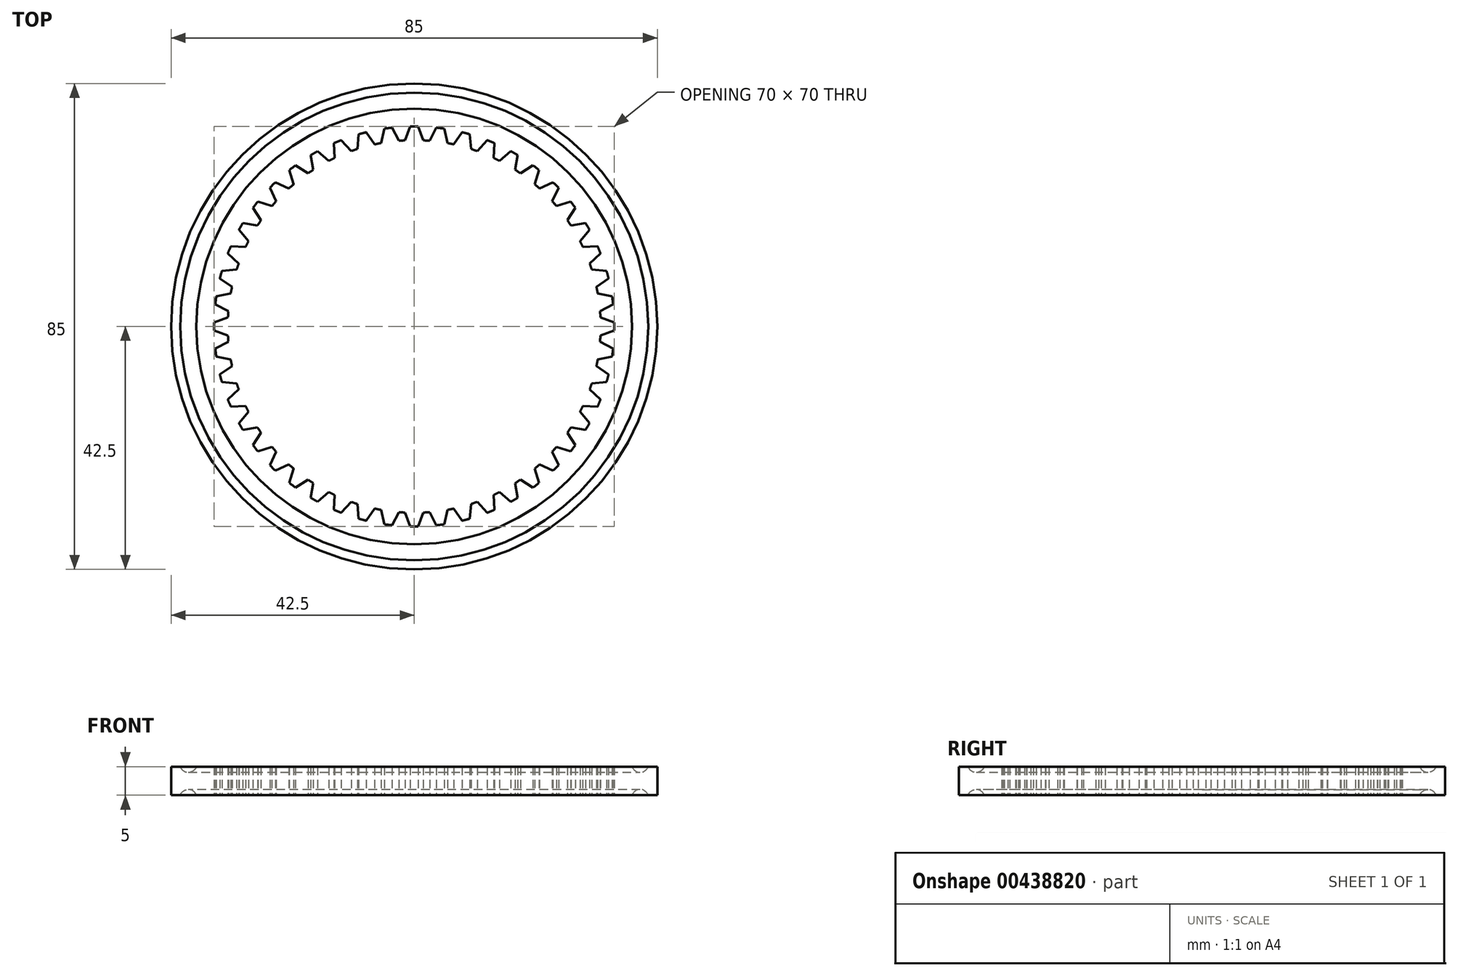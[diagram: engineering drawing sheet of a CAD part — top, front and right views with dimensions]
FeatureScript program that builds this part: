
annotation { "Feature Type Name" : "Feature", "Feature Type Description" : "" }
export const myFeature = defineFeature(function(context is Context, id is Id, definition is map)
    precondition{}
    {
        {
            var Q0;
            Q0=qCreatedBy(makeId("Top.planeOp"),FACE);
            var sketch = newSketch(context, id + "F0", { "sketchPlane" : qUnion([Q0])});
            skCircle(sketch, "E0", {"center": v(0, 0) * mm, "radius": 42.5 * mm});
            skCircle(sketch, "E1", {"center": v(0, 0) * mm, "radius": 34 * mm, "construction": true});
            skCircle(sketch, "E2", {"center": v(0, 0) * mm, "radius": 32.6 * mm, "construction": true});
            skCircle(sketch, "E3", {"center": v(0, 0) * mm, "radius": 35 * mm, "construction": true});
            skLineSegment(sketch, "E4", {"start": v(-1.57, 32.56) * mm, "end": v(-0.69, 35) * mm});
            skLineSegment(sketch, "E5.MirrorCS", {"start": v(1.57, 32.56) * mm, "end": v(0.69, 35) * mm});
            skLineSegment(sketch, "E6.1.0", {"start": v(-5.8, 32.08) * mm, "end": v(-5.25, 34.6) * mm});
            skLineSegment(sketch, "E6.1.1", {"start": v(-2.7, 32.49) * mm, "end": v(-3.89, 34.78) * mm});
            skLineSegment(sketch, "E7.1.2.0", {"start": v(-9.94, 31.05) * mm, "end": v(-9.72, 33.62) * mm});
            skLineSegment(sketch, "E7.3.2.0", {"start": v(-6.91, 31.86) * mm, "end": v(-8.4, 33.98) * mm});
            skLineSegment(sketch, "E7.1.3.0", {"start": v(-13.91, 29.48) * mm, "end": v(-14.03, 32.07) * mm});
            skLineSegment(sketch, "E7.3.3.0", {"start": v(-11, 30.68) * mm, "end": v(-12.76, 32.6) * mm});
            skLineSegment(sketch, "E7.1.4.0", {"start": v(-17.64, 27.41) * mm, "end": v(-18.1, 29.96) * mm});
            skLineSegment(sketch, "E7.3.4.0", {"start": v(-14.92, 28.99) * mm, "end": v(-16.9, 30.65) * mm});
            skLineSegment(sketch, "E7.1.5.0", {"start": v(-21.07, 24.88) * mm, "end": v(-21.85, 27.34) * mm});
            skLineSegment(sketch, "E7.3.5.0", {"start": v(-18.58, 26.79) * mm, "end": v(-20.76, 28.18) * mm});
            skLineSegment(sketch, "E7.1.6.0", {"start": v(-24.14, 21.91) * mm, "end": v(-25.23, 24.26) * mm});
            skLineSegment(sketch, "E7.3.6.0", {"start": v(-21.91, 24.14) * mm, "end": v(-24.26, 25.23) * mm});
            skLineSegment(sketch, "E7.1.7.0", {"start": v(-26.79, 18.58) * mm, "end": v(-28.18, 20.76) * mm});
            skLineSegment(sketch, "E7.3.7.0", {"start": v(-24.88, 21.07) * mm, "end": v(-27.34, 21.85) * mm});
            skLineSegment(sketch, "E7.1.8.0", {"start": v(-28.99, 14.92) * mm, "end": v(-30.65, 16.9) * mm});
            skLineSegment(sketch, "E7.3.8.0", {"start": v(-27.41, 17.64) * mm, "end": v(-29.96, 18.1) * mm});
            skLineSegment(sketch, "E7.1.9.0", {"start": v(-30.68, 11) * mm, "end": v(-32.6, 12.76) * mm});
            skLineSegment(sketch, "E7.3.9.0", {"start": v(-29.48, 13.91) * mm, "end": v(-32.07, 14.03) * mm});
            skLineSegment(sketch, "E7.1.10.0", {"start": v(-31.86, 6.91) * mm, "end": v(-33.98, 8.4) * mm});
            skLineSegment(sketch, "E7.3.10.0", {"start": v(-31.05, 9.94) * mm, "end": v(-33.62, 9.72) * mm});
            skLineSegment(sketch, "E7.1.11.0", {"start": v(-32.49, 2.7) * mm, "end": v(-34.78, 3.89) * mm});
            skLineSegment(sketch, "E7.3.11.0", {"start": v(-32.08, 5.8) * mm, "end": v(-34.6, 5.25) * mm});
            skLineSegment(sketch, "E7.1.12.0", {"start": v(-32.56, -1.57) * mm, "end": v(-35, -0.69) * mm});
            skLineSegment(sketch, "E7.3.12.0", {"start": v(-32.56, 1.57) * mm, "end": v(-35, 0.69) * mm});
            skLineSegment(sketch, "E7.1.13.0", {"start": v(-32.08, -5.8) * mm, "end": v(-34.6, -5.25) * mm});
            skLineSegment(sketch, "E7.3.13.0", {"start": v(-32.49, -2.7) * mm, "end": v(-34.78, -3.89) * mm});
            skLineSegment(sketch, "E7.1.14.0", {"start": v(-31.05, -9.94) * mm, "end": v(-33.62, -9.72) * mm});
            skLineSegment(sketch, "E7.3.14.0", {"start": v(-31.86, -6.91) * mm, "end": v(-33.98, -8.4) * mm});
            skLineSegment(sketch, "E7.1.15.0", {"start": v(-29.48, -13.91) * mm, "end": v(-32.07, -14.03) * mm});
            skLineSegment(sketch, "E7.3.15.0", {"start": v(-30.68, -11) * mm, "end": v(-32.6, -12.76) * mm});
            skLineSegment(sketch, "E7.1.16.0", {"start": v(-27.41, -17.64) * mm, "end": v(-29.96, -18.1) * mm});
            skLineSegment(sketch, "E7.3.16.0", {"start": v(-28.99, -14.92) * mm, "end": v(-30.65, -16.9) * mm});
            skLineSegment(sketch, "E7.1.17.0", {"start": v(-24.88, -21.07) * mm, "end": v(-27.34, -21.85) * mm});
            skLineSegment(sketch, "E7.3.17.0", {"start": v(-26.79, -18.58) * mm, "end": v(-28.18, -20.76) * mm});
            skLineSegment(sketch, "E7.1.18.0", {"start": v(-21.91, -24.14) * mm, "end": v(-24.26, -25.23) * mm});
            skLineSegment(sketch, "E7.3.18.0", {"start": v(-24.14, -21.91) * mm, "end": v(-25.23, -24.26) * mm});
            skLineSegment(sketch, "E7.1.19.0", {"start": v(-18.58, -26.79) * mm, "end": v(-20.76, -28.18) * mm});
            skLineSegment(sketch, "E7.3.19.0", {"start": v(-21.07, -24.88) * mm, "end": v(-21.85, -27.34) * mm});
            skLineSegment(sketch, "E7.1.20.0", {"start": v(-14.92, -28.99) * mm, "end": v(-16.9, -30.65) * mm});
            skLineSegment(sketch, "E7.3.20.0", {"start": v(-17.64, -27.41) * mm, "end": v(-18.1, -29.96) * mm});
            skLineSegment(sketch, "E7.1.21.0", {"start": v(-11, -30.68) * mm, "end": v(-12.76, -32.6) * mm});
            skLineSegment(sketch, "E7.3.21.0", {"start": v(-13.91, -29.48) * mm, "end": v(-14.03, -32.07) * mm});
            skLineSegment(sketch, "E7.1.22.0", {"start": v(-6.91, -31.86) * mm, "end": v(-8.4, -33.98) * mm});
            skLineSegment(sketch, "E7.3.22.0", {"start": v(-9.94, -31.05) * mm, "end": v(-9.72, -33.62) * mm});
            skLineSegment(sketch, "E7.1.23.0", {"start": v(-2.7, -32.49) * mm, "end": v(-3.89, -34.78) * mm});
            skLineSegment(sketch, "E7.3.23.0", {"start": v(-5.8, -32.08) * mm, "end": v(-5.25, -34.6) * mm});
            skLineSegment(sketch, "E7.1.24.0", {"start": v(1.57, -32.56) * mm, "end": v(0.69, -35) * mm});
            skLineSegment(sketch, "E7.3.24.0", {"start": v(-1.57, -32.56) * mm, "end": v(-0.69, -35) * mm});
            skLineSegment(sketch, "E7.1.25.0", {"start": v(5.8, -32.08) * mm, "end": v(5.25, -34.6) * mm});
            skLineSegment(sketch, "E7.3.25.0", {"start": v(2.7, -32.49) * mm, "end": v(3.89, -34.78) * mm});
            skLineSegment(sketch, "E7.1.26.0", {"start": v(9.94, -31.05) * mm, "end": v(9.72, -33.62) * mm});
            skLineSegment(sketch, "E7.3.26.0", {"start": v(6.91, -31.86) * mm, "end": v(8.4, -33.98) * mm});
            skLineSegment(sketch, "E7.1.27.0", {"start": v(13.91, -29.48) * mm, "end": v(14.03, -32.07) * mm});
            skLineSegment(sketch, "E7.3.27.0", {"start": v(11, -30.68) * mm, "end": v(12.76, -32.6) * mm});
            skLineSegment(sketch, "E7.1.28.0", {"start": v(17.64, -27.41) * mm, "end": v(18.1, -29.96) * mm});
            skLineSegment(sketch, "E7.3.28.0", {"start": v(14.92, -28.99) * mm, "end": v(16.9, -30.65) * mm});
            skLineSegment(sketch, "E7.1.29.0", {"start": v(21.07, -24.88) * mm, "end": v(21.85, -27.34) * mm});
            skLineSegment(sketch, "E7.3.29.0", {"start": v(18.58, -26.79) * mm, "end": v(20.76, -28.18) * mm});
            skLineSegment(sketch, "E7.1.30.0", {"start": v(24.14, -21.91) * mm, "end": v(25.23, -24.26) * mm});
            skLineSegment(sketch, "E7.3.30.0", {"start": v(21.91, -24.14) * mm, "end": v(24.26, -25.23) * mm});
            skLineSegment(sketch, "E7.1.31.0", {"start": v(26.79, -18.58) * mm, "end": v(28.18, -20.76) * mm});
            skLineSegment(sketch, "E7.3.31.0", {"start": v(24.88, -21.07) * mm, "end": v(27.34, -21.85) * mm});
            skLineSegment(sketch, "E7.1.32.0", {"start": v(28.99, -14.92) * mm, "end": v(30.65, -16.9) * mm});
            skLineSegment(sketch, "E7.3.32.0", {"start": v(27.41, -17.64) * mm, "end": v(29.96, -18.1) * mm});
            skLineSegment(sketch, "E7.1.33.0", {"start": v(30.68, -11) * mm, "end": v(32.6, -12.76) * mm});
            skLineSegment(sketch, "E7.3.33.0", {"start": v(29.48, -13.91) * mm, "end": v(32.07, -14.03) * mm});
            skLineSegment(sketch, "E7.1.34.0", {"start": v(31.86, -6.91) * mm, "end": v(33.98, -8.4) * mm});
            skLineSegment(sketch, "E7.3.34.0", {"start": v(31.05, -9.94) * mm, "end": v(33.62, -9.72) * mm});
            skLineSegment(sketch, "E7.1.35.0", {"start": v(32.49, -2.7) * mm, "end": v(34.78, -3.89) * mm});
            skLineSegment(sketch, "E7.3.35.0", {"start": v(32.08, -5.8) * mm, "end": v(34.6, -5.25) * mm});
            skLineSegment(sketch, "E7.1.36.0", {"start": v(32.56, 1.57) * mm, "end": v(35, 0.69) * mm});
            skLineSegment(sketch, "E7.3.36.0", {"start": v(32.56, -1.57) * mm, "end": v(35, -0.69) * mm});
            skLineSegment(sketch, "E7.1.37.0", {"start": v(32.08, 5.8) * mm, "end": v(34.6, 5.25) * mm});
            skLineSegment(sketch, "E7.3.37.0", {"start": v(32.49, 2.7) * mm, "end": v(34.78, 3.89) * mm});
            skLineSegment(sketch, "E7.1.38.0", {"start": v(31.05, 9.94) * mm, "end": v(33.62, 9.72) * mm});
            skLineSegment(sketch, "E7.3.38.0", {"start": v(31.86, 6.91) * mm, "end": v(33.98, 8.4) * mm});
            skLineSegment(sketch, "E7.1.39.0", {"start": v(29.48, 13.91) * mm, "end": v(32.07, 14.03) * mm});
            skLineSegment(sketch, "E7.3.39.0", {"start": v(30.68, 11) * mm, "end": v(32.6, 12.76) * mm});
            skLineSegment(sketch, "E7.1.40.0", {"start": v(27.41, 17.64) * mm, "end": v(29.96, 18.1) * mm});
            skLineSegment(sketch, "E7.3.40.0", {"start": v(28.99, 14.92) * mm, "end": v(30.65, 16.9) * mm});
            skLineSegment(sketch, "E7.1.41.0", {"start": v(24.88, 21.07) * mm, "end": v(27.34, 21.85) * mm});
            skLineSegment(sketch, "E7.3.41.0", {"start": v(26.79, 18.58) * mm, "end": v(28.18, 20.76) * mm});
            skLineSegment(sketch, "E7.1.42.0", {"start": v(21.91, 24.14) * mm, "end": v(24.26, 25.23) * mm});
            skLineSegment(sketch, "E7.3.42.0", {"start": v(24.14, 21.91) * mm, "end": v(25.23, 24.26) * mm});
            skLineSegment(sketch, "E7.1.43.0", {"start": v(18.58, 26.79) * mm, "end": v(20.76, 28.18) * mm});
            skLineSegment(sketch, "E7.3.43.0", {"start": v(21.07, 24.88) * mm, "end": v(21.85, 27.34) * mm});
            skLineSegment(sketch, "E7.1.44.0", {"start": v(14.92, 28.99) * mm, "end": v(16.9, 30.65) * mm});
            skLineSegment(sketch, "E7.3.44.0", {"start": v(17.64, 27.41) * mm, "end": v(18.1, 29.96) * mm});
            skLineSegment(sketch, "E7.1.45.0", {"start": v(11, 30.68) * mm, "end": v(12.76, 32.6) * mm});
            skLineSegment(sketch, "E7.3.45.0", {"start": v(13.91, 29.48) * mm, "end": v(14.03, 32.07) * mm});
            skLineSegment(sketch, "E7.1.46.0", {"start": v(6.91, 31.86) * mm, "end": v(8.4, 33.98) * mm});
            skLineSegment(sketch, "E7.3.46.0", {"start": v(9.94, 31.05) * mm, "end": v(9.72, 33.62) * mm});
            skLineSegment(sketch, "E7.1.47.0", {"start": v(2.7, 32.49) * mm, "end": v(3.89, 34.78) * mm});
            skLineSegment(sketch, "E7.3.47.0", {"start": v(5.8, 32.08) * mm, "end": v(5.25, 34.6) * mm});
            skArc(sketch, "E8", {"start": v(1.57, 32.56) * mm, "mid": v(2.13, 32.53) * mm, "end": v(2.7, 32.49) * mm});
            skArc(sketch, "E9", {"start": v(-0.69, 35) * mm, "mid": v(0, 35) * mm, "end": v(0.69, 35) * mm});
            skArc(sketch, "E10.1.0", {"start": v(-5.25, 34.6) * mm, "mid": v(-4.57, 34.7) * mm, "end": v(-3.89, 34.78) * mm});
            skArc(sketch, "E10.1.1", {"start": v(-2.7, 32.49) * mm, "mid": v(-2.13, 32.53) * mm, "end": v(-1.57, 32.56) * mm});
            skArc(sketch, "E10.2.0", {"start": v(-9.72, 33.62) * mm, "mid": v(-9.06, 33.8) * mm, "end": v(-8.4, 33.98) * mm});
            skArc(sketch, "E10.2.1", {"start": v(-6.91, 31.86) * mm, "mid": v(-6.36, 31.97) * mm, "end": v(-5.8, 32.08) * mm});
            skArc(sketch, "E10.3.0", {"start": v(-14.03, 32.07) * mm, "mid": v(-13.4, 32.34) * mm, "end": v(-12.76, 32.6) * mm});
            skArc(sketch, "E10.3.1", {"start": v(-11, 30.68) * mm, "mid": v(-10.48, 30.87) * mm, "end": v(-9.94, 31.05) * mm});
            skArc(sketch, "E10.4.0", {"start": v(-18.1, 29.96) * mm, "mid": v(-17.5, 30.31) * mm, "end": v(-16.9, 30.65) * mm});
            skArc(sketch, "E10.4.1", {"start": v(-14.92, 28.99) * mm, "mid": v(-14.42, 29.24) * mm, "end": v(-13.91, 29.48) * mm});
            skArc(sketch, "E10.5.0", {"start": v(-21.85, 27.34) * mm, "mid": v(-21.3, 27.77) * mm, "end": v(-20.76, 28.18) * mm});
            skArc(sketch, "E10.5.1", {"start": v(-18.58, 26.79) * mm, "mid": v(-18.11, 27.1) * mm, "end": v(-17.64, 27.41) * mm});
            skArc(sketch, "E10.6.0", {"start": v(-25.23, 24.26) * mm, "mid": v(-24.75, 24.75) * mm, "end": v(-24.26, 25.23) * mm});
            skArc(sketch, "E10.6.1", {"start": v(-21.91, 24.14) * mm, "mid": v(-21.5, 24.5) * mm, "end": v(-21.07, 24.88) * mm});
            skArc(sketch, "E10.7.0", {"start": v(-28.18, 20.76) * mm, "mid": v(-27.77, 21.3) * mm, "end": v(-27.34, 21.85) * mm});
            skArc(sketch, "E10.7.1", {"start": v(-24.88, 21.07) * mm, "mid": v(-24.5, 21.5) * mm, "end": v(-24.14, 21.91) * mm});
            skArc(sketch, "E10.8.0", {"start": v(-30.65, 16.9) * mm, "mid": v(-30.31, 17.5) * mm, "end": v(-29.96, 18.1) * mm});
            skArc(sketch, "E10.8.1", {"start": v(-27.41, 17.64) * mm, "mid": v(-27.1, 18.11) * mm, "end": v(-26.79, 18.58) * mm});
            skArc(sketch, "E10.9.0", {"start": v(-32.6, 12.76) * mm, "mid": v(-32.34, 13.4) * mm, "end": v(-32.07, 14.03) * mm});
            skArc(sketch, "E10.9.1", {"start": v(-29.48, 13.91) * mm, "mid": v(-29.24, 14.42) * mm, "end": v(-28.99, 14.92) * mm});
            skArc(sketch, "E10.10.0", {"start": v(-33.98, 8.4) * mm, "mid": v(-33.8, 9.06) * mm, "end": v(-33.62, 9.72) * mm});
            skArc(sketch, "E10.10.1", {"start": v(-31.05, 9.94) * mm, "mid": v(-30.87, 10.48) * mm, "end": v(-30.68, 11) * mm});
            skArc(sketch, "E10.11.0", {"start": v(-34.78, 3.89) * mm, "mid": v(-34.7, 4.57) * mm, "end": v(-34.6, 5.25) * mm});
            skArc(sketch, "E10.11.1", {"start": v(-32.08, 5.8) * mm, "mid": v(-31.97, 6.36) * mm, "end": v(-31.86, 6.91) * mm});
            skArc(sketch, "E10.12.0", {"start": v(-35, -0.69) * mm, "mid": v(-35, 0) * mm, "end": v(-35, 0.69) * mm});
            skArc(sketch, "E10.12.1", {"start": v(-32.56, 1.57) * mm, "mid": v(-32.53, 2.13) * mm, "end": v(-32.49, 2.7) * mm});
            skArc(sketch, "E10.13.0", {"start": v(-34.6, -5.25) * mm, "mid": v(-34.7, -4.57) * mm, "end": v(-34.78, -3.89) * mm});
            skArc(sketch, "E10.13.1", {"start": v(-32.49, -2.7) * mm, "mid": v(-32.53, -2.13) * mm, "end": v(-32.56, -1.57) * mm});
            skArc(sketch, "E10.14.0", {"start": v(-33.62, -9.72) * mm, "mid": v(-33.8, -9.06) * mm, "end": v(-33.98, -8.4) * mm});
            skArc(sketch, "E10.14.1", {"start": v(-31.86, -6.91) * mm, "mid": v(-31.97, -6.36) * mm, "end": v(-32.08, -5.8) * mm});
            skArc(sketch, "E10.15.0", {"start": v(-32.07, -14.03) * mm, "mid": v(-32.34, -13.4) * mm, "end": v(-32.6, -12.76) * mm});
            skArc(sketch, "E10.15.1", {"start": v(-30.68, -11) * mm, "mid": v(-30.87, -10.48) * mm, "end": v(-31.05, -9.94) * mm});
            skArc(sketch, "E10.16.0", {"start": v(-29.96, -18.1) * mm, "mid": v(-30.31, -17.5) * mm, "end": v(-30.65, -16.9) * mm});
            skArc(sketch, "E10.16.1", {"start": v(-28.99, -14.92) * mm, "mid": v(-29.24, -14.42) * mm, "end": v(-29.48, -13.91) * mm});
            skArc(sketch, "E10.17.0", {"start": v(-27.34, -21.85) * mm, "mid": v(-27.77, -21.3) * mm, "end": v(-28.18, -20.76) * mm});
            skArc(sketch, "E10.17.1", {"start": v(-26.79, -18.58) * mm, "mid": v(-27.1, -18.11) * mm, "end": v(-27.41, -17.64) * mm});
            skArc(sketch, "E10.18.0", {"start": v(-24.26, -25.23) * mm, "mid": v(-24.75, -24.75) * mm, "end": v(-25.23, -24.26) * mm});
            skArc(sketch, "E10.18.1", {"start": v(-24.14, -21.91) * mm, "mid": v(-24.5, -21.5) * mm, "end": v(-24.88, -21.07) * mm});
            skArc(sketch, "E10.19.0", {"start": v(-20.76, -28.18) * mm, "mid": v(-21.3, -27.77) * mm, "end": v(-21.85, -27.34) * mm});
            skArc(sketch, "E10.19.1", {"start": v(-21.07, -24.88) * mm, "mid": v(-21.5, -24.5) * mm, "end": v(-21.91, -24.14) * mm});
            skArc(sketch, "E10.20.0", {"start": v(-16.9, -30.65) * mm, "mid": v(-17.5, -30.31) * mm, "end": v(-18.1, -29.96) * mm});
            skArc(sketch, "E10.20.1", {"start": v(-17.64, -27.41) * mm, "mid": v(-18.11, -27.1) * mm, "end": v(-18.58, -26.79) * mm});
            skArc(sketch, "E10.21.0", {"start": v(-12.76, -32.6) * mm, "mid": v(-13.4, -32.34) * mm, "end": v(-14.03, -32.07) * mm});
            skArc(sketch, "E10.21.1", {"start": v(-13.91, -29.48) * mm, "mid": v(-14.42, -29.24) * mm, "end": v(-14.92, -28.99) * mm});
            skArc(sketch, "E10.22.0", {"start": v(-8.4, -33.98) * mm, "mid": v(-9.06, -33.8) * mm, "end": v(-9.72, -33.62) * mm});
            skArc(sketch, "E10.22.1", {"start": v(-9.94, -31.05) * mm, "mid": v(-10.48, -30.87) * mm, "end": v(-11, -30.68) * mm});
            skArc(sketch, "E10.23.0", {"start": v(-3.89, -34.78) * mm, "mid": v(-4.57, -34.7) * mm, "end": v(-5.25, -34.6) * mm});
            skArc(sketch, "E10.23.1", {"start": v(-5.8, -32.08) * mm, "mid": v(-6.36, -31.97) * mm, "end": v(-6.91, -31.86) * mm});
            skArc(sketch, "E10.24.0", {"start": v(0.69, -35) * mm, "mid": v(0, -35) * mm, "end": v(-0.69, -35) * mm});
            skArc(sketch, "E10.24.1", {"start": v(-1.57, -32.56) * mm, "mid": v(-2.13, -32.53) * mm, "end": v(-2.7, -32.49) * mm});
            skArc(sketch, "E10.25.0", {"start": v(5.25, -34.6) * mm, "mid": v(4.57, -34.7) * mm, "end": v(3.89, -34.78) * mm});
            skArc(sketch, "E10.25.1", {"start": v(2.7, -32.49) * mm, "mid": v(2.13, -32.53) * mm, "end": v(1.57, -32.56) * mm});
            skArc(sketch, "E10.26.0", {"start": v(9.72, -33.62) * mm, "mid": v(9.06, -33.8) * mm, "end": v(8.4, -33.98) * mm});
            skArc(sketch, "E10.26.1", {"start": v(6.91, -31.86) * mm, "mid": v(6.36, -31.97) * mm, "end": v(5.8, -32.08) * mm});
            skArc(sketch, "E10.27.0", {"start": v(14.03, -32.07) * mm, "mid": v(13.4, -32.34) * mm, "end": v(12.76, -32.6) * mm});
            skArc(sketch, "E10.27.1", {"start": v(11, -30.68) * mm, "mid": v(10.48, -30.87) * mm, "end": v(9.94, -31.05) * mm});
            skArc(sketch, "E10.28.0", {"start": v(18.1, -29.96) * mm, "mid": v(17.5, -30.31) * mm, "end": v(16.9, -30.65) * mm});
            skArc(sketch, "E10.28.1", {"start": v(14.92, -28.99) * mm, "mid": v(14.42, -29.24) * mm, "end": v(13.91, -29.48) * mm});
            skArc(sketch, "E10.29.0", {"start": v(21.85, -27.34) * mm, "mid": v(21.3, -27.77) * mm, "end": v(20.76, -28.18) * mm});
            skArc(sketch, "E10.29.1", {"start": v(18.58, -26.79) * mm, "mid": v(18.11, -27.1) * mm, "end": v(17.64, -27.41) * mm});
            skArc(sketch, "E10.30.0", {"start": v(25.23, -24.26) * mm, "mid": v(24.75, -24.75) * mm, "end": v(24.26, -25.23) * mm});
            skArc(sketch, "E10.30.1", {"start": v(21.91, -24.14) * mm, "mid": v(21.5, -24.5) * mm, "end": v(21.07, -24.88) * mm});
            skArc(sketch, "E10.31.0", {"start": v(28.18, -20.76) * mm, "mid": v(27.77, -21.3) * mm, "end": v(27.34, -21.85) * mm});
            skArc(sketch, "E10.31.1", {"start": v(24.88, -21.07) * mm, "mid": v(24.5, -21.5) * mm, "end": v(24.14, -21.91) * mm});
            skArc(sketch, "E10.32.0", {"start": v(30.65, -16.9) * mm, "mid": v(30.31, -17.5) * mm, "end": v(29.96, -18.1) * mm});
            skArc(sketch, "E10.32.1", {"start": v(27.41, -17.64) * mm, "mid": v(27.1, -18.11) * mm, "end": v(26.79, -18.58) * mm});
            skArc(sketch, "E10.33.0", {"start": v(32.6, -12.76) * mm, "mid": v(32.34, -13.4) * mm, "end": v(32.07, -14.03) * mm});
            skArc(sketch, "E10.33.1", {"start": v(29.48, -13.91) * mm, "mid": v(29.24, -14.42) * mm, "end": v(28.99, -14.92) * mm});
            skArc(sketch, "E10.34.0", {"start": v(33.98, -8.4) * mm, "mid": v(33.8, -9.06) * mm, "end": v(33.62, -9.72) * mm});
            skArc(sketch, "E10.34.1", {"start": v(31.05, -9.94) * mm, "mid": v(30.87, -10.48) * mm, "end": v(30.68, -11) * mm});
            skArc(sketch, "E10.35.0", {"start": v(34.78, -3.89) * mm, "mid": v(34.7, -4.57) * mm, "end": v(34.6, -5.25) * mm});
            skArc(sketch, "E10.35.1", {"start": v(32.08, -5.8) * mm, "mid": v(31.97, -6.36) * mm, "end": v(31.86, -6.91) * mm});
            skArc(sketch, "E10.36.0", {"start": v(35, 0.69) * mm, "mid": v(35, 0) * mm, "end": v(35, -0.69) * mm});
            skArc(sketch, "E10.36.1", {"start": v(32.56, -1.57) * mm, "mid": v(32.53, -2.13) * mm, "end": v(32.49, -2.7) * mm});
            skArc(sketch, "E10.37.0", {"start": v(34.6, 5.25) * mm, "mid": v(34.7, 4.57) * mm, "end": v(34.78, 3.89) * mm});
            skArc(sketch, "E10.37.1", {"start": v(32.49, 2.7) * mm, "mid": v(32.53, 2.13) * mm, "end": v(32.56, 1.57) * mm});
            skArc(sketch, "E10.38.0", {"start": v(33.62, 9.72) * mm, "mid": v(33.8, 9.06) * mm, "end": v(33.98, 8.4) * mm});
            skArc(sketch, "E10.38.1", {"start": v(31.86, 6.91) * mm, "mid": v(31.97, 6.36) * mm, "end": v(32.08, 5.8) * mm});
            skArc(sketch, "E10.39.0", {"start": v(32.07, 14.03) * mm, "mid": v(32.34, 13.4) * mm, "end": v(32.6, 12.76) * mm});
            skArc(sketch, "E10.39.1", {"start": v(30.68, 11) * mm, "mid": v(30.87, 10.48) * mm, "end": v(31.05, 9.94) * mm});
            skArc(sketch, "E10.40.0", {"start": v(29.96, 18.1) * mm, "mid": v(30.31, 17.5) * mm, "end": v(30.65, 16.9) * mm});
            skArc(sketch, "E10.40.1", {"start": v(28.99, 14.92) * mm, "mid": v(29.24, 14.42) * mm, "end": v(29.48, 13.91) * mm});
            skArc(sketch, "E10.41.0", {"start": v(27.34, 21.85) * mm, "mid": v(27.77, 21.3) * mm, "end": v(28.18, 20.76) * mm});
            skArc(sketch, "E10.41.1", {"start": v(26.79, 18.58) * mm, "mid": v(27.1, 18.11) * mm, "end": v(27.41, 17.64) * mm});
            skArc(sketch, "E10.42.0", {"start": v(24.26, 25.23) * mm, "mid": v(24.75, 24.75) * mm, "end": v(25.23, 24.26) * mm});
            skArc(sketch, "E10.42.1", {"start": v(24.14, 21.91) * mm, "mid": v(24.5, 21.5) * mm, "end": v(24.88, 21.07) * mm});
            skArc(sketch, "E10.43.0", {"start": v(20.76, 28.18) * mm, "mid": v(21.3, 27.77) * mm, "end": v(21.85, 27.34) * mm});
            skArc(sketch, "E10.43.1", {"start": v(21.07, 24.88) * mm, "mid": v(21.5, 24.5) * mm, "end": v(21.91, 24.14) * mm});
            skArc(sketch, "E10.44.0", {"start": v(16.9, 30.65) * mm, "mid": v(17.5, 30.31) * mm, "end": v(18.1, 29.96) * mm});
            skArc(sketch, "E10.44.1", {"start": v(17.64, 27.41) * mm, "mid": v(18.11, 27.1) * mm, "end": v(18.58, 26.79) * mm});
            skArc(sketch, "E10.45.0", {"start": v(12.76, 32.6) * mm, "mid": v(13.4, 32.34) * mm, "end": v(14.03, 32.07) * mm});
            skArc(sketch, "E10.45.1", {"start": v(13.91, 29.48) * mm, "mid": v(14.42, 29.24) * mm, "end": v(14.92, 28.99) * mm});
            skArc(sketch, "E10.46.0", {"start": v(8.4, 33.98) * mm, "mid": v(9.06, 33.8) * mm, "end": v(9.72, 33.62) * mm});
            skArc(sketch, "E10.46.1", {"start": v(9.94, 31.05) * mm, "mid": v(10.48, 30.87) * mm, "end": v(11, 30.68) * mm});
            skArc(sketch, "E10.47.0", {"start": v(3.89, 34.78) * mm, "mid": v(4.57, 34.7) * mm, "end": v(5.25, 34.6) * mm});
            skArc(sketch, "E10.47.1", {"start": v(5.8, 32.08) * mm, "mid": v(6.36, 31.97) * mm, "end": v(6.91, 31.86) * mm});
            skSolve(sketch);
        }
        {
            var Q0;
            Q0 = qSketchRegion(id + "F0", true);
            extrude(context, id + "F1", {"entities" : qUnion([Q0]), "depth" : 5 * mm});
        }
        {
            var Q0;
            Q0=qCreatedBy(makeId("Front.planeOp"),FACE);
            var sketch = newSketch(context, id + "F2", { "sketchPlane" : qUnion([Q0])});
            skLineSegment(sketch, "E11", {"start": v(-42.5, 0) * mm, "end": v(-42.5, 5) * mm});
            skCircle(sketch, "E12", {"center": v(-39.5, 5.5) * mm, "radius": 1.5 * mm});
            skCircle(sketch, "E13", {"center": v(-39.5, -0.5) * mm, "radius": 1.5 * mm});
            skSolve(sketch);
        }
        {
            var Q0;
            Q0 = qSketchRegion(id + "F2", true);
            var Q1;
            Q1=makeQuery(id+"F1.opExtrude","CAP_EDGE",EDGE,{"disambiguationData":[OSD([sQuery(id+"F0.wireOp",EDGE,"E0")])],"isStart":false});
            revolve(context, id + "F3", {"operationType" : NewBodyOperationType.REMOVE, "entities" : qUnion([Q0]), "axis" : qUnion([Q1]), "revolveType" : RevolveType.FULL, "oppositeDirection" : true});
        }
    });
